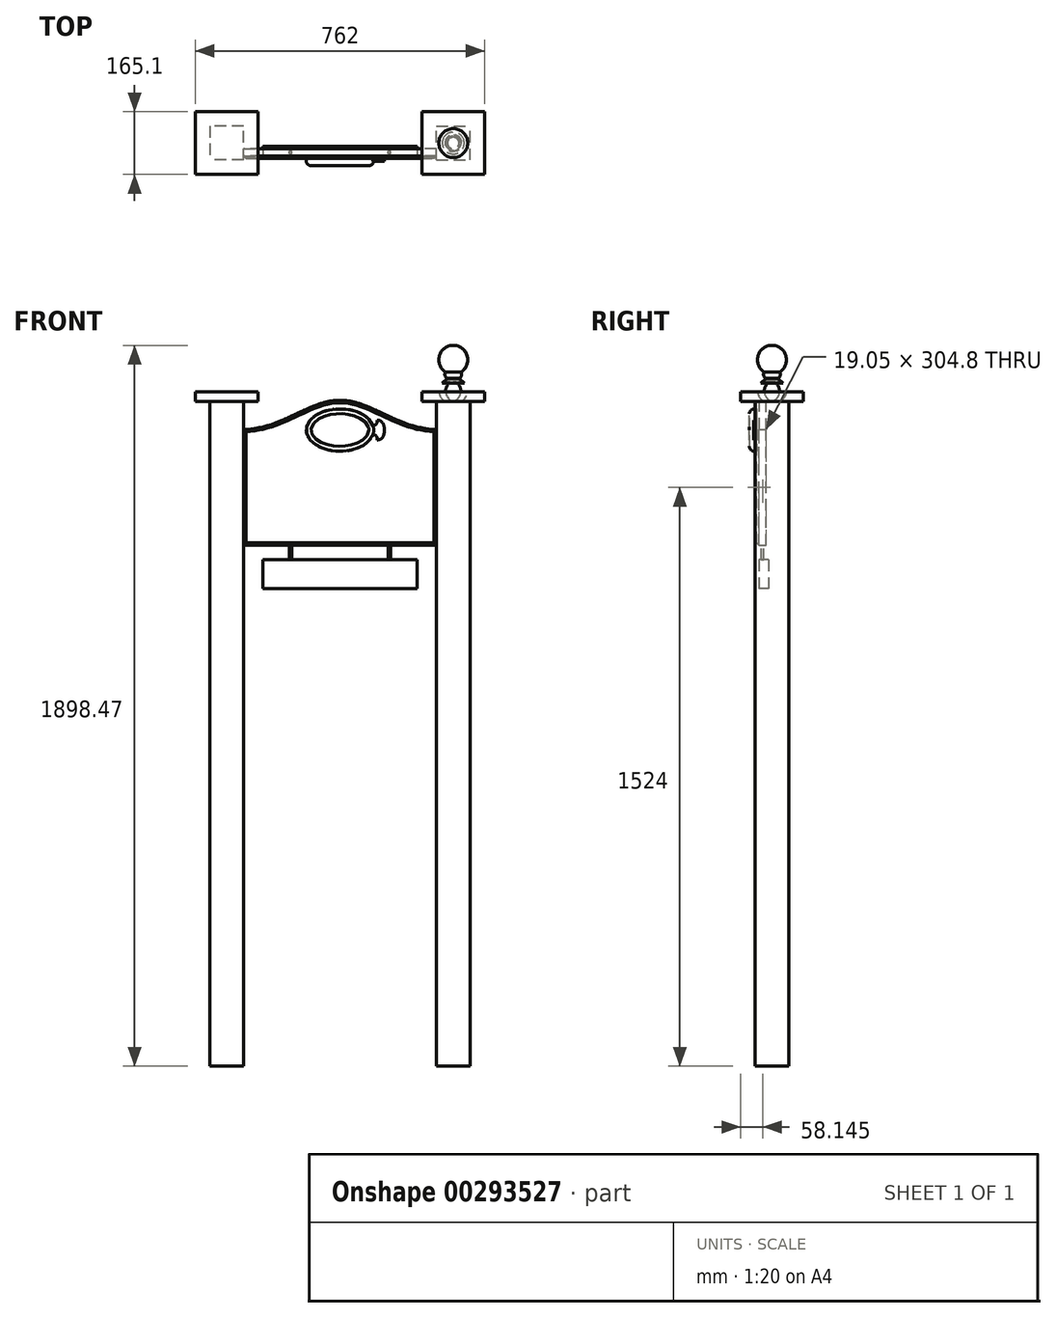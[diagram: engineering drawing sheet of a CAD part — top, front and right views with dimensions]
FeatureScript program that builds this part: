
annotation { "Feature Type Name" : "Feature", "Feature Type Description" : "" }
export const myFeature = defineFeature(function(context is Context, id is Id, definition is map)
    precondition{}
    {
        {
            var Q0;
            Q0=qCreatedBy(makeId("Front.planeOp"),FACE);
            var sketch = newSketch(context, id + "F0", { "sketchPlane" : qUnion([Q0])});
            skLineSegment(sketch, "E0", {"start": v(0, 0) * mm, "end": v(254, 0) * mm});
            skLineSegment(sketch, "E1", {"start": v(254, 0) * mm, "end": v(254, 304.8) * mm});
            skLineSegment(sketch, "E2", {"start": v(0, 0) * mm, "end": v(0, 381.75) * mm, "construction": true});
            skFitSpline(sketch, "E3", {"points": [v(254, 304.8) * mm, v(177.05, 319.7) * mm, v(57.9, 371) * mm, v(0, 381.75) * mm], "startDerivative": vector(-225.05, 21.98) * mm, "endDerivative": vector(-190.28, 0) * mm});
            skFitSpline(sketch, "E4.MirrorCS", {"points": [v(-254, 304.8) * mm, v(-177.05, 319.7) * mm, v(-57.9, 371) * mm, v(0, 381.75) * mm], "startDerivative": vector(225.05, 21.98) * mm, "endDerivative": vector(190.28, 0) * mm});
            skLineSegment(sketch, "E5.MirrorCS", {"start": v(-254, 0) * mm, "end": v(-254, 304.8) * mm});
            skLineSegment(sketch, "E6.MirrorCS", {"start": v(0, 0) * mm, "end": v(-254, 0) * mm});
            skSolve(sketch);
        }
        {
            var Q0;
            Q0 = qSketchRegion(id + "F0", true);
            extrude(context, id + "F1", {"entities" : qUnion([Q0]), "depth" : 25.4 * mm});
        }
        {
            var Q0;
            Q0=makeQuery(id+"F1.opExtrude","CAP_FACE",FACE,{"disambiguationData":[OSD([sQuery(id+"F0.wireOp",EDGE,"E0"),sQuery(id+"F0.wireOp",EDGE,"E1"),sQuery(id+"F0.wireOp",EDGE,"E3"),sQuery(id+"F0.wireOp",EDGE,"E4.MirrorCS"),sQuery(id+"F0.wireOp",EDGE,"E5.MirrorCS"),sQuery(id+"F0.wireOp",EDGE,"E6.MirrorCS")])],"isStart":false});
            var sketch = newSketch(context, id + "F2", { "sketchPlane" : qUnion([Q0])});
            skEllipse(sketch, "E7", {"center": v(0, 303.76) * mm, "majorRadius": 89.02 * mm, "minorRadius": 55.73 * mm, "majorAxis": v(1, 0)});
            skSolve(sketch);
        }
        {
            var Q0;
            Q0 = qSketchRegion(id + "F2", true);
            extrude(context, id + "F3", {"entities" : qUnion([Q0]), "operationType" : NewBodyOperationType.ADD, "depth" : 19.05 * mm});
        }
        {
            var Q0;
            Q0=makeQuery(id+"F3.opExtrude","CAP_EDGE",EDGE,{"disambiguationData":[OSD([sQuery(id+"F2.wireOp",EDGE,"E7")])],"isStart":false});
            fillet(context, id + "F4", {"entities" : qUnion([Q0]), "radius" : 12.7 * mm, "tangentPropagation" : true, "allowEdgeOverflow" : false});
        }
        {
            var Q0;
            Q0=makeQuery(id+"F1.opExtrude","CAP_EDGE",EDGE,{"disambiguationData":[OSD([sQuery(id+"F0.wireOp",EDGE,"E4.MirrorCS")])],"isStart":false});
            var Q1;
            Q1=makeQuery(id+"F1.opExtrude","CAP_EDGE",EDGE,{"disambiguationData":[OSD([sQuery(id+"F0.wireOp",EDGE,"E1")])],"isStart":false});
            var Q2;
            Q2=makeQuery(id+"F1.opExtrude","CAP_EDGE",EDGE,{"disambiguationData":[OSD([sQuery(id+"F0.wireOp",EDGE,"E0"),sQuery(id+"F0.wireOp",EDGE,"E6.MirrorCS")])],"isStart":false});
            var Q3;
            Q3=makeQuery(id+"F1.opExtrude","CAP_EDGE",EDGE,{"disambiguationData":[OSD([sQuery(id+"F0.wireOp",EDGE,"E5.MirrorCS")])],"isStart":false});
            chamfer(context, id + "F5", {"entities" : qUnion([Q0, Q1, Q2, Q3]), "width" : 6.35 * mm, "tangentPropagation" : true});
        }
        {
            var Q0;
            Q0=makeQuery(id+"F1.opExtrude","CAP_FACE",FACE,{"disambiguationData":[OSD([sQuery(id+"F0.wireOp",EDGE,"E0"),sQuery(id+"F0.wireOp",EDGE,"E1"),sQuery(id+"F0.wireOp",EDGE,"E3"),sQuery(id+"F0.wireOp",EDGE,"E4.MirrorCS"),sQuery(id+"F0.wireOp",EDGE,"E5.MirrorCS"),sQuery(id+"F0.wireOp",EDGE,"E6.MirrorCS")])],"isStart":false});
            var sketch = newSketch(context, id + "F6", { "sketchPlane" : qUnion([Q0])});
            skLineSegment(sketch, "E8", {"start": v(0, 375.4) * mm, "end": v(0, 202.71) * mm, "construction": true});
            skPoint(sketch, "E8.endSnap0", {"position": v(0, 359.5) * mm});
            skLineSegment(sketch, "E9", {"start": v(116.92, 303.76) * mm, "end": v(89.02, 303.76) * mm, "construction": true});
            skPoint(sketch, "E9.endSnap0", {"position": v(89.02, 303.76) * mm});
            skFitSpline(sketch, "E10", {"points": [v(86.84, 316.02) * mm, v(94.56, 317.94) * mm, v(98.41, 329.83) * mm], "startDerivative": vector(24.36, 4.16) * mm, "endDerivative": vector(1.9, 28.1) * mm});
            skFitSpline(sketch, "E11", {"points": [v(98.41, 329.83) * mm, v(110.92, 324.62) * mm, v(116.92, 303.76) * mm], "startDerivative": vector(31.85, -3.49) * mm, "endDerivative": vector(0, -44.7) * mm});
            skFitSpline(sketch, "E12.MirrorCS", {"points": [v(98.41, 277.7) * mm, v(110.92, 282.91) * mm, v(116.92, 303.76) * mm], "startDerivative": vector(31.85, 3.49) * mm, "endDerivative": vector(0, 44.7) * mm});
            skFitSpline(sketch, "E13.MirrorCS", {"points": [v(86.84, 291.5) * mm, v(94.56, 289.59) * mm, v(98.41, 277.7) * mm], "startDerivative": vector(24.36, -4.16) * mm, "endDerivative": vector(1.9, -28.1) * mm});
            skSolve(sketch);
        }
        {
            var Q0;
            {var subQ1=sQuery(id+"F6.wireOp",EDGE,"E10");Q0=makeQuery(id+"F6.imprint","IMPRINT",FACE,{"disambiguationData":[TD([[makeQuery(id+"F6.imprint","IMPRINT",EDGE,{"derivedFrom":subQ1}),-1.0]])]});}
            extrude(context, id + "F7", {"entities" : qUnion([Q0]), "operationType" : NewBodyOperationType.ADD, "depth" : 7.62 * mm});
        }
        {
            var Q0;
            Q0=makeQuery(id+"F1.opExtrude","SWEPT_FACE",FACE,{"disambiguationData":[OSD([sQuery(id+"F0.wireOp",EDGE,"E0"),sQuery(id+"F0.wireOp",EDGE,"E6.MirrorCS")])]});
            var sketch = newSketch(context, id + "F8", { "sketchPlane" : qUnion([Q0])});
            skPoint(sketch, "E14.firstSnap0", {"position": v(-254, 9.53) * mm});
            skLineSegment(sketch, "E14.bottom", {"start": v(-254, -59.33) * mm, "end": v(-342.9, -59.33) * mm});
            skLineSegment(sketch, "E14.top", {"start": v(-254, 29.57) * mm, "end": v(-342.9, 29.57) * mm});
            skLineSegment(sketch, "E14.left", {"start": v(-254, -59.33) * mm, "end": v(-254, 29.57) * mm});
            skLineSegment(sketch, "E14.right", {"start": v(-342.9, -59.33) * mm, "end": v(-342.9, 29.57) * mm});
            skLineSegment(sketch, "E15.bottom", {"start": v(254, 29.57) * mm, "end": v(342.9, 29.57) * mm});
            skLineSegment(sketch, "E15.top", {"start": v(254, -59.33) * mm, "end": v(342.9, -59.33) * mm});
            skLineSegment(sketch, "E15.left", {"start": v(254, 29.57) * mm, "end": v(254, -59.33) * mm});
            skLineSegment(sketch, "E15.right", {"start": v(342.9, 29.57) * mm, "end": v(342.9, -59.33) * mm});
            skSolve(sketch);
        }
        {
            var Q0;
            Q0 = qSketchRegion(id + "F8", true);
            extrude(context, id + "F9", {"entities" : qUnion([Q0]), "operationType" : NewBodyOperationType.ADD, "oppositeDirection" : true, "depth" : 378.46 * mm, "hasSecondDirection" : true, "secondDirectionOppositeDirection" : false, "secondDirectionDepth" : 1371.6 * mm});
        }
        {
            var Q0;
            Q0=makeQuery(id+"F9.opExtrude","CAP_FACE",FACE,{"disambiguationData":[OSD([sQuery(id+"F8.wireOp",EDGE,"E15.bottom"),sQuery(id+"F8.wireOp",EDGE,"E15.top"),sQuery(id+"F8.wireOp",EDGE,"E15.left"),sQuery(id+"F8.wireOp",EDGE,"E15.right")])],"isStart":false});
            var sketch = newSketch(context, id + "F10", { "sketchPlane" : qUnion([Q0])});
            skLineSegment(sketch, "E16.0", {"start": v(215.9, 97.43) * mm, "end": v(215.9, -67.67) * mm});
            skLineSegment(sketch, "E16.1", {"start": v(381, 97.43) * mm, "end": v(215.9, 97.43) * mm});
            skLineSegment(sketch, "E16.2", {"start": v(381, -67.67) * mm, "end": v(381, 97.43) * mm});
            skLineSegment(sketch, "E16.3", {"start": v(215.9, -67.67) * mm, "end": v(381, -67.67) * mm});
            skLineSegment(sketch, "E17.0", {"start": v(-215.9, -67.67) * mm, "end": v(-215.9, 97.43) * mm});
            skLineSegment(sketch, "E17.1", {"start": v(-381, -67.67) * mm, "end": v(-215.9, -67.67) * mm});
            skLineSegment(sketch, "E17.2", {"start": v(-381, 97.43) * mm, "end": v(-381, -67.67) * mm});
            skLineSegment(sketch, "E17.3", {"start": v(-215.9, 97.43) * mm, "end": v(-381, 97.43) * mm});
            skSolve(sketch);
        }
        {
            var Q0;
            Q0 = qSketchRegion(id + "F10", true);
            extrude(context, id + "F11", {"entities" : qUnion([Q0]), "operationType" : NewBodyOperationType.ADD, "depth" : 25.4 * mm});
        }
        {
            var Q0;
            Q0=makeQuery(id+"F11.opExtrude","CAP_FACE",FACE,{"disambiguationData":[OSD([sQuery(id+"F10.wireOp",EDGE,"E16.0"),sQuery(id+"F10.wireOp",EDGE,"E16.1"),sQuery(id+"F10.wireOp",EDGE,"E16.2"),sQuery(id+"F10.wireOp",EDGE,"E16.3")])],"isStart":false});
            var sketch = newSketch(context, id + "F12", { "sketchPlane" : qUnion([Q0])});
            skLineSegment(sketch, "E18", {"start": v(215.9, -67.67) * mm, "end": v(381, 97.43) * mm, "construction": true});
            skLineSegment(sketch, "E19.bottom", {"start": v(298.45, 14.88) * mm, "end": v(285.95, 14.88) * mm});
            skLineSegment(sketch, "E19.top", {"start": v(298.45, 28.67) * mm, "end": v(285.95, 28.67) * mm});
            skLineSegment(sketch, "E19.left", {"start": v(298.45, 14.88) * mm, "end": v(298.45, 28.67) * mm});
            skLineSegment(sketch, "E19.right", {"start": v(285.95, 14.88) * mm, "end": v(285.95, 28.67) * mm});
            skSolve(sketch);
        }
        {
            var Q0;
            Q0=makeQuery(id+"F12.imprint","IMPRINT",FACE,{"disambiguationData":[TD([[makeQuery(id+"F12.imprint","IMPRINT",EDGE,{"derivedFrom":sQuery(id+"F12.wireOp",EDGE,"E19.bottom")}),-1.0]])]});
            extrude(context, id + "F13", {"entities" : qUnion([Q0]), "operationType" : NewBodyOperationType.ADD, "depth" : 101.6 * mm});
        }
        {
            var Q0;
            Q0=makeQuery(id+"F13.opExtrude","SWEPT_FACE",FACE,{"disambiguationData":[OSD([sQuery(id+"F12.wireOp",EDGE,"E19.bottom")])]});
            var sketch = newSketch(context, id + "F14", { "sketchPlane" : qUnion([Q0])});
            skArc(sketch, "E20", {"start": v(335.98, 403.86) * mm, "mid": v(334.2, 416.25) * mm, "end": v(327.35, 426.73) * mm});
            skLineSegment(sketch, "E21", {"start": v(327.35, 426.73) * mm, "end": v(313.7, 440) * mm});
            skArc(sketch, "E22", {"start": v(313.7, 440) * mm, "mid": v(320.26, 447) * mm, "end": v(318.62, 456.45) * mm});
            skArc(sketch, "E23", {"start": v(318.62, 456.45) * mm, "mid": v(335.08, 499.26) * mm, "end": v(298.45, 526.87) * mm});
            skLineSegment(sketch, "E24", {"start": v(298.45, 526.87) * mm, "end": v(298.45, 403.86) * mm});
            skLineSegment(sketch, "E25", {"start": v(298.45, 403.86) * mm, "end": v(335.98, 403.86) * mm});
            skSolve(sketch);
        }
        {
            var Q0;
            Q0=makeQuery(id+"F14.imprint","IMPRINT",FACE,{"disambiguationData":[TD([[makeQuery(id+"F14.imprint","IMPRINT",EDGE,{"derivedFrom":sQuery(id+"F14.wireOp",EDGE,"E20")}),1.0]])]});
            var Q1;
            Q1=sQuery(id+"F14.wireOp",EDGE,"E24");
            revolve(context, id + "F15", {"operationType" : NewBodyOperationType.ADD, "entities" : qUnion([Q0]), "axis" : qUnion([Q1]), "revolveType" : RevolveType.FULL});
        }
        {
            var Q0;
            Q0=makeQuery(id+"F1.opExtrude","SWEPT_FACE",FACE,{"disambiguationData":[OSD([sQuery(id+"F0.wireOp",EDGE,"E0"),sQuery(id+"F0.wireOp",EDGE,"E6.MirrorCS")])]});
            var sketch = newSketch(context, id + "F16", { "sketchPlane" : qUnion([Q0])});
            skLineSegment(sketch, "E26.bottom", {"start": v(-133.35, 12.7) * mm, "end": v(-127, 12.7) * mm});
            skLineSegment(sketch, "E26.top", {"start": v(-133.35, 6.35) * mm, "end": v(-127, 6.35) * mm});
            skLineSegment(sketch, "E26.left", {"start": v(-133.35, 12.7) * mm, "end": v(-133.35, 6.35) * mm});
            skLineSegment(sketch, "E26.right", {"start": v(-127, 12.7) * mm, "end": v(-127, 6.35) * mm});
            skLineSegment(sketch, "E27.MirrorCS", {"start": v(127, 12.7) * mm, "end": v(127, 6.35) * mm});
            skLineSegment(sketch, "E28.MirrorCS", {"start": v(133.35, 12.7) * mm, "end": v(133.35, 6.35) * mm});
            skLineSegment(sketch, "E29.MirrorCS", {"start": v(133.35, 6.35) * mm, "end": v(127, 6.35) * mm});
            skLineSegment(sketch, "E30.MirrorCS", {"start": v(133.35, 12.7) * mm, "end": v(127, 12.7) * mm});
            skSolve(sketch);
        }
        {
            var Q0;
            Q0 = qSketchRegion(id + "F16", true);
            extrude(context, id + "F17", {"entities" : qUnion([Q0]), "operationType" : NewBodyOperationType.ADD, "depth" : 76.2 * mm});
        }
        {
            var Q0;
            Q0=makeQuery(id+"F1.opExtrude","CAP_FACE",FACE,{"disambiguationData":[OSD([sQuery(id+"F0.wireOp",EDGE,"E0"),sQuery(id+"F0.wireOp",EDGE,"E1"),sQuery(id+"F0.wireOp",EDGE,"E3"),sQuery(id+"F0.wireOp",EDGE,"E4.MirrorCS"),sQuery(id+"F0.wireOp",EDGE,"E5.MirrorCS"),sQuery(id+"F0.wireOp",EDGE,"E6.MirrorCS")])],"isStart":false});
            var Q1;
            {var subQ0=sQuery(id+"F0.wireOp",EDGE,"E5.MirrorCS");var subQ1=sQuery(id+"F0.wireOp",EDGE,"E6.MirrorCS");var subQ2=sQuery(id+"F0.wireOp",EDGE,"E0");Q1=makeQuery(id+"F5.opChamfer","BLEND_VERTEX",VERTEX,{"blendedFrom":[makeQuery(id+"F1.opExtrude","CAP_EDGE",EDGE,{"disambiguationData":[OSD([subQ2,subQ1])],"isStart":false}),makeQuery(id+"F1.opExtrude","CAP_EDGE",EDGE,{"disambiguationData":[OSD([subQ0])],"isStart":false}),makeQuery(id+"F1.opExtrude","SWEPT_FACE",FACE,{"disambiguationData":[OSD([subQ2,subQ1])]}),makeQuery(id+"F1.opExtrude","SWEPT_FACE",FACE,{"disambiguationData":[OSD([subQ0])]})],"blendedInto":[makeQuery(id+"F1.opExtrude","SWEPT_FACE",FACE,{"disambiguationData":[OSD([subQ2,subQ1])]}),makeQuery(id+"F1.opExtrude","SWEPT_FACE",FACE,{"disambiguationData":[OSD([subQ0])]})]});}
            cPlane(context, id + "F18", {"entities" : qUnion([Q0, Q1]), "cplaneType" : CPlaneType.PLANE_POINT, "offset" : 25.4 * mm, "width" : 152.4 * mm, "height" : 152.4 * mm});
        }
        {
            var Q0;
            Q0=qCreatedBy(id+"F18.planeOp",FACE);
            var sketch = newSketch(context, id + "F19", { "sketchPlane" : qUnion([Q0])});
            skLineSegment(sketch, "E31.bottom", {"start": v(-203.2, -38.1) * mm, "end": v(203.2, -38.1) * mm});
            skLineSegment(sketch, "E31.top", {"start": v(-203.2, -114.3) * mm, "end": v(203.2, -114.3) * mm});
            skLineSegment(sketch, "E31.left", {"start": v(-203.2, -38.1) * mm, "end": v(-203.2, -114.3) * mm});
            skLineSegment(sketch, "E31.right", {"start": v(203.2, -38.1) * mm, "end": v(203.2, -114.3) * mm});
            skSolve(sketch);
        }
        {
            var Q0;
            Q0 = qSketchRegion(id + "F19", true);
            extrude(context, id + "F20", {"entities" : qUnion([Q0]), "operationType" : NewBodyOperationType.ADD, "oppositeDirection" : true, "depth" : 25.4 * mm});
        }
    });
